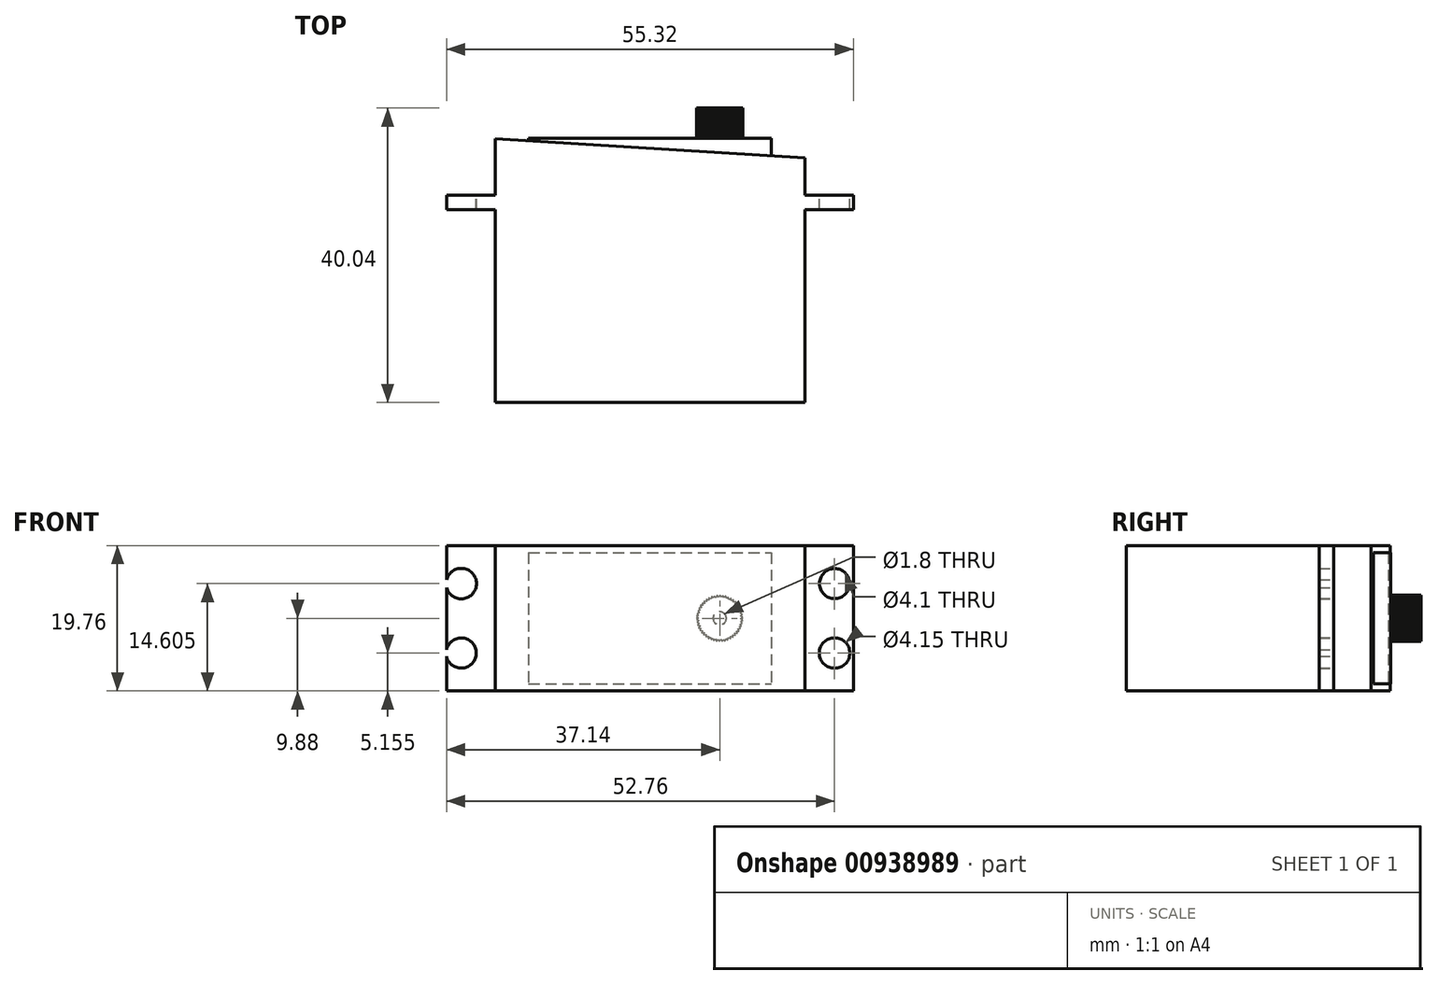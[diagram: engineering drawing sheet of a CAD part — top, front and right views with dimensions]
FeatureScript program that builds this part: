
annotation { "Feature Type Name" : "Feature", "Feature Type Description" : "" }
export const myFeature = defineFeature(function(context is Context, id is Id, definition is map)
    precondition{}
    {
        {
            var Q0;
            Q0=qCreatedBy(makeId("Top.planeOp"),FACE);
            var sketch = newSketch(context, id + "F0", { "sketchPlane" : qUnion([Q0])});
            skLineSegment(sketch, "E0", {"start": v(-4.56, 0) * mm, "end": v(37.56, 0) * mm});
            skLineSegment(sketch, "E1", {"start": v(-4.56, 0) * mm, "end": v(-4.56, 26.2) * mm});
            skLineSegment(sketch, "E2", {"start": v(37.56, 0) * mm, "end": v(37.56, 26.2) * mm});
            skLineSegment(sketch, "E3", {"start": v(-4.56, 35.9) * mm, "end": v(37.56, 33.29) * mm});
            skLineSegment(sketch, "E4", {"start": v(37.56, 0) * mm, "end": v(37.56, 26.2) * mm, "construction": true});
            skLineSegment(sketch, "E5", {"start": v(37.56, 26.2) * mm, "end": v(-4.56, 26.2) * mm, "construction": true});
            skLineSegment(sketch, "E6.bottom", {"start": v(-4.56, 26.2) * mm, "end": v(-11.16, 26.2) * mm});
            skLineSegment(sketch, "E6.top", {"start": v(-4.56, 28.2) * mm, "end": v(-11.16, 28.2) * mm});
            skLineSegment(sketch, "E6.right", {"start": v(-11.16, 26.2) * mm, "end": v(-11.16, 28.2) * mm});
            skLineSegment(sketch, "E7.bottom", {"start": v(37.56, 26.2) * mm, "end": v(44.16, 26.2) * mm});
            skLineSegment(sketch, "E7.top", {"start": v(37.56, 28.2) * mm, "end": v(44.16, 28.2) * mm});
            skLineSegment(sketch, "E7.right", {"start": v(44.16, 26.2) * mm, "end": v(44.16, 28.2) * mm});
            skLineSegment(sketch, "E8.trimOffspring", {"start": v(37.56, 28.2) * mm, "end": v(37.56, 33.29) * mm});
            skLineSegment(sketch, "E9.trimOffspring", {"start": v(-4.56, 28.2) * mm, "end": v(-4.56, 35.9) * mm});
            skLineSegment(sketch, "E10", {"start": v(16.5, 0) * mm, "end": v(16.5, 35.9) * mm, "construction": true});
            skLineSegment(sketch, "E11", {"start": v(0, 35.9) * mm, "end": v(33, 35.9) * mm});
            skLineSegment(sketch, "E12", {"start": v(0, 35.9) * mm, "end": v(0, 35.62) * mm});
            skLineSegment(sketch, "E13", {"start": v(33, 35.9) * mm, "end": v(33, 33.57) * mm});
            skLineSegment(sketch, "E14", {"start": v(37.56, 28.2) * mm, "end": v(-4.56, 28.2) * mm, "construction": true});
            skSolve(sketch);
        }
        {
            var Q0;
            Q0=makeQuery(id+"F0.imprint","IMPRINT",FACE,{"disambiguationData":[TD([[makeQuery(id+"F0.imprint","IMPRINT",EDGE,{"derivedFrom":sQuery(id+"F0.wireOp",EDGE,"E0")}),1.0]])]});
            extrude(context, id + "F1", {"entities" : qUnion([Q0]), "depth" : 19.77 * mm, "offsetDistance" : 25 * mm, "symmetric" : true});
        }
        {
            var Q0;
            Q0=makeQuery(id+"F0.imprint","IMPRINT",FACE,{"disambiguationData":[TD([[makeQuery(id+"F0.imprint","IMPRINT",EDGE,{"derivedFrom":sQuery(id+"F0.wireOp",EDGE,"E11")}),-1.0]])]});
            extrude(context, id + "F2", {"entities" : qUnion([Q0]), "operationType" : NewBodyOperationType.ADD, "depth" : 17.8 * mm, "offsetDistance" : 25 * mm, "symmetric" : true});
        }
        {
            var Q0;
            Q0=makeQuery(id+"F1.opExtrude","SWEPT_FACE",FACE,{"disambiguationData":[OSD([sQuery(id+"F0.wireOp",EDGE,"E7.top")])]});
            var sketch = newSketch(context, id + "F3", { "sketchPlane" : qUnion([Q0])});
            skLineSegment(sketch, "E15", {"start": v(11.16, -4.72) * mm, "end": v(11.16, 4.72) * mm, "construction": true});
            skLineSegment(sketch, "E16", {"start": v(11.16, 4.72) * mm, "end": v(9.16, 4.72) * mm, "construction": true});
            skLineSegment(sketch, "E17", {"start": v(9.16, 4.72) * mm, "end": v(9.16, -4.72) * mm, "construction": true});
            skLineSegment(sketch, "E18", {"start": v(11.16, -4.72) * mm, "end": v(9.16, -4.72) * mm, "construction": true});
            skCircle(sketch, "E19", {"center": v(9.16, -4.72) * mm, "radius": 2.05 * mm});
            skCircle(sketch, "E20", {"center": v(9.16, 4.72) * mm, "radius": 2.08 * mm});
            skLineSegment(sketch, "E21", {"start": v(-43.6, 4.72) * mm, "end": v(-43.6, -4.72) * mm, "construction": true});
            skLineSegment(sketch, "E22", {"start": v(-43.6, -4.72) * mm, "end": v(-41.6, -4.72) * mm, "construction": true});
            skLineSegment(sketch, "E23", {"start": v(-41.6, -4.72) * mm, "end": v(-41.6, 4.73) * mm, "construction": true});
            skLineSegment(sketch, "E24", {"start": v(-43.6, 4.72) * mm, "end": v(-41.6, 4.72) * mm, "construction": true});
            skCircle(sketch, "E25", {"center": v(-41.6, 4.73) * mm, "radius": 2.05 * mm});
            skCircle(sketch, "E26", {"center": v(-41.6, -4.72) * mm, "radius": 2.08 * mm});
            skSolve(sketch);
        }
        {
            var Q0;
            {var subQ0=sQuery(id+"F3.wireOp",EDGE,"E25");var subQ1=makeQuery(id+"F1.opExtrude","SWEPT_EDGE",EDGE,{"disambiguationData":[OSD([sQuery(id+"F0.wireOp",EDGE,"E7.top"),sQuery(id+"F0.wireOp",EDGE,"E7.right")])]});var subQ2=makeQuery(id+"F3.imprint","INTERSECT",VERTEX,{"disambiguationData":[OD(0.0)],"derivedFrom":[subQ1,subQ0]});Q0=makeQuery(id+"F3.imprint","IMPRINT",FACE,{"disambiguationData":[TD([[makeQuery(id+"F3.imprint","IMPRINT",EDGE,{"disambiguationData":[TD([[subQ2,1.0]])],"derivedFrom":subQ0}),1.0]])]});}
            var Q1;
            {var subQ0=sQuery(id+"F3.wireOp",EDGE,"E26");var subQ1=makeQuery(id+"F1.opExtrude","SWEPT_EDGE",EDGE,{"disambiguationData":[OSD([sQuery(id+"F0.wireOp",EDGE,"E7.top"),sQuery(id+"F0.wireOp",EDGE,"E7.right")])]});var subQ2=makeQuery(id+"F3.imprint","INTERSECT",VERTEX,{"disambiguationData":[OD(0.0)],"derivedFrom":[subQ1,subQ0]});Q1=makeQuery(id+"F3.imprint","IMPRINT",FACE,{"disambiguationData":[TD([[makeQuery(id+"F3.imprint","IMPRINT",EDGE,{"disambiguationData":[TD([[subQ2,-1.0]])],"derivedFrom":subQ0}),1.0]])]});}
            var Q2;
            Q2=makeQuery(id+"F3.imprint","IMPRINT",FACE,{"disambiguationData":[TD([[makeQuery(id+"F3.imprint","IMPRINT",EDGE,{"derivedFrom":sQuery(id+"F3.wireOp",EDGE,"E20")}),1.0]])]});
            var Q3;
            Q3=makeQuery(id+"F3.imprint","IMPRINT",FACE,{"disambiguationData":[TD([[makeQuery(id+"F3.imprint","IMPRINT",EDGE,{"derivedFrom":sQuery(id+"F3.wireOp",EDGE,"E19")}),1.0]])]});
            extrude(context, id + "F4", {"entities" : qUnion([Q0, Q1, Q2, Q3]), "operationType" : NewBodyOperationType.REMOVE, "oppositeDirection" : true, "depth" : 25 * mm, "offsetDistance" : 25 * mm});
        }
        {
            var Q0;
            Q0=makeQuery(id+"F2.opExtrude","SWEPT_FACE",FACE,{"disambiguationData":[OSD([sQuery(id+"F0.wireOp",EDGE,"E11")])]});
            var sketch = newSketch(context, id + "F5", { "sketchPlane" : qUnion([Q0])});
            skLineSegment(sketch, "E27", {"start": v(-33, 0) * mm, "end": v(-25.98, 0) * mm, "construction": true});
            skCircle(sketch, "E28", {"center": v(-25.98, 0) * mm, "radius": 2.9 * mm});
            skLineSegment(sketch, "E29", {"start": v(-26.2, 2.9) * mm, "end": v(-26.03, 3.14) * mm});
            skLineSegment(sketch, "E30", {"start": v(-26.03, 3.14) * mm, "end": v(-25.87, 2.9) * mm});
            skLineSegment(sketch, "E31.1.0", {"start": v(-26.56, 2.84) * mm, "end": v(-26.42, 3.1) * mm});
            skLineSegment(sketch, "E31.1.1", {"start": v(-26.42, 3.1) * mm, "end": v(-26.23, 2.89) * mm});
            skLineSegment(sketch, "E31.2.0", {"start": v(-26.91, 2.75) * mm, "end": v(-26.8, 3.03) * mm});
            skLineSegment(sketch, "E31.2.1", {"start": v(-26.8, 3.03) * mm, "end": v(-26.59, 2.84) * mm});
            skLineSegment(sketch, "E31.3.0", {"start": v(-27.25, 2.6) * mm, "end": v(-27.18, 2.9) * mm});
            skLineSegment(sketch, "E31.3.1", {"start": v(-27.18, 2.9) * mm, "end": v(-26.94, 2.74) * mm});
            skLineSegment(sketch, "E31.4.0", {"start": v(-27.57, 2.43) * mm, "end": v(-27.53, 2.73) * mm});
            skLineSegment(sketch, "E31.4.1", {"start": v(-27.53, 2.73) * mm, "end": v(-27.28, 2.6) * mm});
            skLineSegment(sketch, "E31.5.0", {"start": v(-27.86, 2.21) * mm, "end": v(-27.86, 2.51) * mm});
            skLineSegment(sketch, "E31.5.1", {"start": v(-27.86, 2.51) * mm, "end": v(-27.6, 2.41) * mm});
            skLineSegment(sketch, "E31.6.0", {"start": v(-28.12, 1.96) * mm, "end": v(-28.16, 2.26) * mm});
            skLineSegment(sketch, "E31.6.1", {"start": v(-28.16, 2.26) * mm, "end": v(-27.88, 2.2) * mm});
            skLineSegment(sketch, "E31.7.0", {"start": v(-28.35, 1.67) * mm, "end": v(-28.43, 1.96) * mm});
            skLineSegment(sketch, "E31.7.1", {"start": v(-28.43, 1.96) * mm, "end": v(-28.14, 1.94) * mm});
            skLineSegment(sketch, "E31.8.0", {"start": v(-28.54, 1.36) * mm, "end": v(-28.66, 1.64) * mm});
            skLineSegment(sketch, "E31.8.1", {"start": v(-28.66, 1.64) * mm, "end": v(-28.37, 1.65) * mm});
            skLineSegment(sketch, "E31.9.0", {"start": v(-28.69, 1.03) * mm, "end": v(-28.84, 1.3) * mm});
            skLineSegment(sketch, "E31.9.1", {"start": v(-28.84, 1.3) * mm, "end": v(-28.55, 1.34) * mm});
            skLineSegment(sketch, "E31.10.0", {"start": v(-28.8, 0.69) * mm, "end": v(-28.98, 0.92) * mm});
            skLineSegment(sketch, "E31.10.1", {"start": v(-28.98, 0.92) * mm, "end": v(-28.7, 1) * mm});
            skLineSegment(sketch, "E31.11.0", {"start": v(-28.86, 0.33) * mm, "end": v(-29.07, 0.54) * mm});
            skLineSegment(sketch, "E31.11.1", {"start": v(-29.07, 0.54) * mm, "end": v(-28.8, 0.66) * mm});
            skLineSegment(sketch, "E32.3.12.0", {"start": v(-29.12, 0.15) * mm, "end": v(-28.87, 0.3) * mm});
            skLineSegment(sketch, "E32.5.12.0", {"start": v(-28.88, -0.04) * mm, "end": v(-29.12, 0.15) * mm});
            skLineSegment(sketch, "E32.3.13.0", {"start": v(-29.11, -0.24) * mm, "end": v(-28.88, -0.07) * mm});
            skLineSegment(sketch, "E32.5.13.0", {"start": v(-28.85, -0.4) * mm, "end": v(-29.11, -0.24) * mm});
            skLineSegment(sketch, "E32.3.14.0", {"start": v(-29.06, -0.64) * mm, "end": v(-28.85, -0.43) * mm});
            skLineSegment(sketch, "E32.5.14.0", {"start": v(-28.78, -0.76) * mm, "end": v(-29.06, -0.64) * mm});
            skLineSegment(sketch, "E32.3.15.0", {"start": v(-28.95, -1.02) * mm, "end": v(-28.77, -0.79) * mm});
            skLineSegment(sketch, "E32.5.15.0", {"start": v(-28.66, -1.1) * mm, "end": v(-28.95, -1.02) * mm});
            skLineSegment(sketch, "E32.3.16.0", {"start": v(-28.8, -1.38) * mm, "end": v(-28.65, -1.13) * mm});
            skLineSegment(sketch, "E32.5.16.0", {"start": v(-28.5, -1.43) * mm, "end": v(-28.8, -1.38) * mm});
            skLineSegment(sketch, "E32.3.17.0", {"start": v(-28.6, -1.72) * mm, "end": v(-28.49, -1.46) * mm});
            skLineSegment(sketch, "E32.5.17.0", {"start": v(-28.3, -1.73) * mm, "end": v(-28.6, -1.72) * mm});
            skLineSegment(sketch, "E32.3.18.0", {"start": v(-28.37, -2.04) * mm, "end": v(-28.29, -1.76) * mm});
            skLineSegment(sketch, "E32.5.18.0", {"start": v(-28.07, -2.01) * mm, "end": v(-28.37, -2.04) * mm});
            skLineSegment(sketch, "E32.3.19.0", {"start": v(-28.1, -2.32) * mm, "end": v(-28.05, -2.03) * mm});
            skLineSegment(sketch, "E32.5.19.0", {"start": v(-27.8, -2.26) * mm, "end": v(-28.1, -2.32) * mm});
            skLineSegment(sketch, "E33.3.20.0", {"start": v(-27.79, -2.57) * mm, "end": v(-27.78, -2.28) * mm});
            skLineSegment(sketch, "E33.5.20.0", {"start": v(-27.5, -2.47) * mm, "end": v(-27.79, -2.57) * mm});
            skLineSegment(sketch, "E33.3.21.0", {"start": v(-27.45, -2.77) * mm, "end": v(-27.48, -2.48) * mm});
            skLineSegment(sketch, "E33.5.21.0", {"start": v(-27.18, -2.64) * mm, "end": v(-27.45, -2.77) * mm});
            skLineSegment(sketch, "E33.3.22.0", {"start": v(-27.1, -2.94) * mm, "end": v(-27.15, -2.65) * mm});
            skLineSegment(sketch, "E33.5.22.0", {"start": v(-26.84, -2.77) * mm, "end": v(-27.1, -2.94) * mm});
            skLineSegment(sketch, "E33.3.23.0", {"start": v(-26.71, -3.05) * mm, "end": v(-26.81, -2.78) * mm});
            skLineSegment(sketch, "E33.5.23.0", {"start": v(-26.49, -2.86) * mm, "end": v(-26.71, -3.05) * mm});
            skLineSegment(sketch, "E33.3.24.0", {"start": v(-26.33, -3.12) * mm, "end": v(-26.46, -2.86) * mm});
            skLineSegment(sketch, "E33.5.24.0", {"start": v(-26.13, -2.9) * mm, "end": v(-26.33, -3.12) * mm});
            skLineSegment(sketch, "E33.3.25.0", {"start": v(-25.93, -3.14) * mm, "end": v(-26.1, -2.9) * mm});
            skLineSegment(sketch, "E33.5.25.0", {"start": v(-25.76, -2.9) * mm, "end": v(-25.93, -3.14) * mm});
            skLineSegment(sketch, "E33.3.26.0", {"start": v(-25.54, -3.1) * mm, "end": v(-25.73, -2.89) * mm});
            skLineSegment(sketch, "E33.5.26.0", {"start": v(-25.4, -2.84) * mm, "end": v(-25.54, -3.1) * mm});
            skLineSegment(sketch, "E33.3.27.0", {"start": v(-25.15, -3.03) * mm, "end": v(-25.37, -2.84) * mm});
            skLineSegment(sketch, "E33.5.27.0", {"start": v(-25.05, -2.75) * mm, "end": v(-25.15, -3.03) * mm});
            skLineSegment(sketch, "E33.3.28.0", {"start": v(-24.78, -2.9) * mm, "end": v(-25.02, -2.74) * mm});
            skLineSegment(sketch, "E33.5.28.0", {"start": v(-24.71, -2.6) * mm, "end": v(-24.78, -2.9) * mm});
            skLineSegment(sketch, "E33.3.29.0", {"start": v(-24.43, -2.73) * mm, "end": v(-24.68, -2.6) * mm});
            skLineSegment(sketch, "E33.5.29.0", {"start": v(-24.4, -2.43) * mm, "end": v(-24.43, -2.73) * mm});
            skLineSegment(sketch, "E33.3.30.0", {"start": v(-24.1, -2.51) * mm, "end": v(-24.37, -2.41) * mm});
            skLineSegment(sketch, "E33.5.30.0", {"start": v(-24.1, -2.21) * mm, "end": v(-24.1, -2.51) * mm});
            skLineSegment(sketch, "E33.3.31.0", {"start": v(-23.8, -2.26) * mm, "end": v(-24.08, -2.2) * mm});
            skLineSegment(sketch, "E33.5.31.0", {"start": v(-23.84, -1.96) * mm, "end": v(-23.8, -2.26) * mm});
            skLineSegment(sketch, "E33.3.32.0", {"start": v(-23.53, -1.96) * mm, "end": v(-23.82, -1.94) * mm});
            skLineSegment(sketch, "E33.5.32.0", {"start": v(-23.61, -1.67) * mm, "end": v(-23.53, -1.96) * mm});
            skLineSegment(sketch, "E33.3.33.0", {"start": v(-23.3, -1.64) * mm, "end": v(-23.6, -1.65) * mm});
            skLineSegment(sketch, "E33.5.33.0", {"start": v(-23.42, -1.36) * mm, "end": v(-23.3, -1.64) * mm});
            skLineSegment(sketch, "E33.3.34.0", {"start": v(-23.12, -1.3) * mm, "end": v(-23.4, -1.34) * mm});
            skLineSegment(sketch, "E33.5.34.0", {"start": v(-23.27, -1.03) * mm, "end": v(-23.12, -1.3) * mm});
            skLineSegment(sketch, "E33.3.35.0", {"start": v(-22.98, -0.92) * mm, "end": v(-23.26, -1) * mm});
            skLineSegment(sketch, "E33.5.35.0", {"start": v(-23.16, -0.69) * mm, "end": v(-22.98, -0.92) * mm});
            skLineSegment(sketch, "E33.3.36.0", {"start": v(-22.89, -0.54) * mm, "end": v(-23.16, -0.66) * mm});
            skLineSegment(sketch, "E33.5.36.0", {"start": v(-23.1, -0.33) * mm, "end": v(-22.89, -0.54) * mm});
            skLineSegment(sketch, "E33.3.37.0", {"start": v(-22.84, -0.15) * mm, "end": v(-23.1, -0.3) * mm});
            skLineSegment(sketch, "E33.5.37.0", {"start": v(-23.08, 0.04) * mm, "end": v(-22.84, -0.15) * mm});
            skLineSegment(sketch, "E33.3.38.0", {"start": v(-22.85, 0.24) * mm, "end": v(-23.08, 0.07) * mm});
            skLineSegment(sketch, "E33.5.38.0", {"start": v(-23.1, 0.4) * mm, "end": v(-22.85, 0.24) * mm});
            skLineSegment(sketch, "E33.3.39.0", {"start": v(-22.9, 0.64) * mm, "end": v(-23.11, 0.43) * mm});
            skLineSegment(sketch, "E33.5.39.0", {"start": v(-23.18, 0.76) * mm, "end": v(-22.9, 0.64) * mm});
            skLineSegment(sketch, "E34.3.40.0", {"start": v(-23, 1.02) * mm, "end": v(-23.19, 0.79) * mm});
            skLineSegment(sketch, "E34.5.40.0", {"start": v(-23.3, 1.1) * mm, "end": v(-23, 1.02) * mm});
            skLineSegment(sketch, "E34.3.41.0", {"start": v(-23.16, 1.38) * mm, "end": v(-23.3, 1.13) * mm});
            skLineSegment(sketch, "E34.5.41.0", {"start": v(-23.46, 1.43) * mm, "end": v(-23.16, 1.38) * mm});
            skLineSegment(sketch, "E34.3.42.0", {"start": v(-23.35, 1.72) * mm, "end": v(-23.47, 1.46) * mm});
            skLineSegment(sketch, "E34.5.42.0", {"start": v(-23.66, 1.73) * mm, "end": v(-23.35, 1.72) * mm});
            skLineSegment(sketch, "E34.3.43.0", {"start": v(-23.6, 2.04) * mm, "end": v(-23.67, 1.76) * mm});
            skLineSegment(sketch, "E34.5.43.0", {"start": v(-23.9, 2.01) * mm, "end": v(-23.6, 2.04) * mm});
            skLineSegment(sketch, "E34.3.44.0", {"start": v(-23.87, 2.32) * mm, "end": v(-23.91, 2.03) * mm});
            skLineSegment(sketch, "E34.5.44.0", {"start": v(-24.16, 2.26) * mm, "end": v(-23.87, 2.32) * mm});
            skLineSegment(sketch, "E35.3.45.0", {"start": v(-24.17, 2.57) * mm, "end": v(-24.18, 2.28) * mm});
            skLineSegment(sketch, "E35.5.45.0", {"start": v(-24.46, 2.47) * mm, "end": v(-24.17, 2.57) * mm});
            skLineSegment(sketch, "E35.3.46.0", {"start": v(-24.5, 2.77) * mm, "end": v(-24.48, 2.48) * mm});
            skLineSegment(sketch, "E35.5.46.0", {"start": v(-24.78, 2.64) * mm, "end": v(-24.5, 2.77) * mm});
            skLineSegment(sketch, "E35.3.47.0", {"start": v(-24.87, 2.94) * mm, "end": v(-24.8, 2.65) * mm});
            skLineSegment(sketch, "E35.5.47.0", {"start": v(-25.12, 2.77) * mm, "end": v(-24.87, 2.94) * mm});
            skLineSegment(sketch, "E35.3.48.0", {"start": v(-25.25, 3.05) * mm, "end": v(-25.15, 2.78) * mm});
            skLineSegment(sketch, "E35.5.48.0", {"start": v(-25.47, 2.86) * mm, "end": v(-25.25, 3.05) * mm});
            skLineSegment(sketch, "E35.3.49.0", {"start": v(-25.63, 3.12) * mm, "end": v(-25.5, 2.86) * mm});
            skLineSegment(sketch, "E35.5.49.0", {"start": v(-25.83, 2.9) * mm, "end": v(-25.63, 3.12) * mm});
            skCircle(sketch, "E36", {"center": v(-25.98, 0) * mm, "radius": 0.9 * mm});
            skSolve(sketch);
        }
        {
            var Q0;
            {var subQ0=sQuery(id+"F5.wireOp",EDGE,"E31.9.0");Q0=makeQuery(id+"F5.imprint","IMPRINT",FACE,{"disambiguationData":[TD([[makeQuery(id+"F5.imprint","IMPRINT",EDGE,{"derivedFrom":subQ0}),-1.0]])]});}
            var Q1;
            {var subQ0=sQuery(id+"F5.wireOp",EDGE,"E31.8.0");Q1=makeQuery(id+"F5.imprint","IMPRINT",FACE,{"disambiguationData":[TD([[makeQuery(id+"F5.imprint","IMPRINT",EDGE,{"derivedFrom":subQ0}),-1.0]])]});}
            var Q2;
            {var subQ0=sQuery(id+"F5.wireOp",EDGE,"E31.7.0");Q2=makeQuery(id+"F5.imprint","IMPRINT",FACE,{"disambiguationData":[TD([[makeQuery(id+"F5.imprint","IMPRINT",EDGE,{"derivedFrom":subQ0}),-1.0]])]});}
            var Q3;
            {var subQ0=sQuery(id+"F5.wireOp",EDGE,"E31.6.0");Q3=makeQuery(id+"F5.imprint","IMPRINT",FACE,{"disambiguationData":[TD([[makeQuery(id+"F5.imprint","IMPRINT",EDGE,{"derivedFrom":subQ0}),-1.0]])]});}
            var Q4;
            {var subQ0=sQuery(id+"F5.wireOp",EDGE,"E31.5.0");Q4=makeQuery(id+"F5.imprint","IMPRINT",FACE,{"disambiguationData":[TD([[makeQuery(id+"F5.imprint","IMPRINT",EDGE,{"derivedFrom":subQ0}),-1.0]])]});}
            var Q5;
            {var subQ0=sQuery(id+"F5.wireOp",EDGE,"E31.4.0");Q5=makeQuery(id+"F5.imprint","IMPRINT",FACE,{"disambiguationData":[TD([[makeQuery(id+"F5.imprint","IMPRINT",EDGE,{"derivedFrom":subQ0}),-1.0]])]});}
            var Q6;
            {var subQ0=sQuery(id+"F5.wireOp",EDGE,"E31.3.0");Q6=makeQuery(id+"F5.imprint","IMPRINT",FACE,{"disambiguationData":[TD([[makeQuery(id+"F5.imprint","IMPRINT",EDGE,{"derivedFrom":subQ0}),-1.0]])]});}
            var Q7;
            {var subQ0=sQuery(id+"F5.wireOp",EDGE,"E31.2.0");Q7=makeQuery(id+"F5.imprint","IMPRINT",FACE,{"disambiguationData":[TD([[makeQuery(id+"F5.imprint","IMPRINT",EDGE,{"derivedFrom":subQ0}),-1.0]])]});}
            var Q8;
            {var subQ0=sQuery(id+"F5.wireOp",EDGE,"E31.1.0");Q8=makeQuery(id+"F5.imprint","IMPRINT",FACE,{"disambiguationData":[TD([[makeQuery(id+"F5.imprint","IMPRINT",EDGE,{"derivedFrom":subQ0}),-1.0]])]});}
            var Q9;
            {var subQ0=sQuery(id+"F5.wireOp",EDGE,"E29");Q9=makeQuery(id+"F5.imprint","IMPRINT",FACE,{"disambiguationData":[TD([[makeQuery(id+"F5.imprint","IMPRINT",EDGE,{"derivedFrom":subQ0}),-1.0]])]});}
            var Q10;
            {var subQ0=sQuery(id+"F5.wireOp",EDGE,"E35.3.49.0");Q10=makeQuery(id+"F5.imprint","IMPRINT",FACE,{"disambiguationData":[TD([[makeQuery(id+"F5.imprint","IMPRINT",EDGE,{"derivedFrom":subQ0}),-1.0]])]});}
            var Q11;
            {var subQ0=sQuery(id+"F5.wireOp",EDGE,"E35.3.48.0");Q11=makeQuery(id+"F5.imprint","IMPRINT",FACE,{"disambiguationData":[TD([[makeQuery(id+"F5.imprint","IMPRINT",EDGE,{"derivedFrom":subQ0}),-1.0]])]});}
            var Q12;
            {var subQ0=sQuery(id+"F5.wireOp",EDGE,"E35.3.47.0");Q12=makeQuery(id+"F5.imprint","IMPRINT",FACE,{"disambiguationData":[TD([[makeQuery(id+"F5.imprint","IMPRINT",EDGE,{"derivedFrom":subQ0}),-1.0]])]});}
            var Q13;
            {var subQ0=sQuery(id+"F5.wireOp",EDGE,"E35.3.46.0");Q13=makeQuery(id+"F5.imprint","IMPRINT",FACE,{"disambiguationData":[TD([[makeQuery(id+"F5.imprint","IMPRINT",EDGE,{"derivedFrom":subQ0}),-1.0]])]});}
            var Q14;
            {var subQ0=sQuery(id+"F5.wireOp",EDGE,"E35.3.45.0");Q14=makeQuery(id+"F5.imprint","IMPRINT",FACE,{"disambiguationData":[TD([[makeQuery(id+"F5.imprint","IMPRINT",EDGE,{"derivedFrom":subQ0}),-1.0]])]});}
            var Q15;
            {var subQ0=sQuery(id+"F5.wireOp",EDGE,"E34.3.44.0");Q15=makeQuery(id+"F5.imprint","IMPRINT",FACE,{"disambiguationData":[TD([[makeQuery(id+"F5.imprint","IMPRINT",EDGE,{"derivedFrom":subQ0}),-1.0]])]});}
            var Q16;
            {var subQ0=sQuery(id+"F5.wireOp",EDGE,"E34.3.43.0");Q16=makeQuery(id+"F5.imprint","IMPRINT",FACE,{"disambiguationData":[TD([[makeQuery(id+"F5.imprint","IMPRINT",EDGE,{"derivedFrom":subQ0}),-1.0]])]});}
            var Q17;
            {var subQ0=sQuery(id+"F5.wireOp",EDGE,"E34.3.42.0");Q17=makeQuery(id+"F5.imprint","IMPRINT",FACE,{"disambiguationData":[TD([[makeQuery(id+"F5.imprint","IMPRINT",EDGE,{"derivedFrom":subQ0}),-1.0]])]});}
            var Q18;
            {var subQ0=sQuery(id+"F5.wireOp",EDGE,"E34.3.41.0");Q18=makeQuery(id+"F5.imprint","IMPRINT",FACE,{"disambiguationData":[TD([[makeQuery(id+"F5.imprint","IMPRINT",EDGE,{"derivedFrom":subQ0}),-1.0]])]});}
            var Q19;
            {var subQ0=sQuery(id+"F5.wireOp",EDGE,"E34.3.40.0");Q19=makeQuery(id+"F5.imprint","IMPRINT",FACE,{"disambiguationData":[TD([[makeQuery(id+"F5.imprint","IMPRINT",EDGE,{"derivedFrom":subQ0}),-1.0]])]});}
            var Q20;
            {var subQ0=sQuery(id+"F5.wireOp",EDGE,"E33.3.39.0");Q20=makeQuery(id+"F5.imprint","IMPRINT",FACE,{"disambiguationData":[TD([[makeQuery(id+"F5.imprint","IMPRINT",EDGE,{"derivedFrom":subQ0}),-1.0]])]});}
            var Q21;
            {var subQ0=sQuery(id+"F5.wireOp",EDGE,"E33.3.38.0");Q21=makeQuery(id+"F5.imprint","IMPRINT",FACE,{"disambiguationData":[TD([[makeQuery(id+"F5.imprint","IMPRINT",EDGE,{"derivedFrom":subQ0}),-1.0]])]});}
            var Q22;
            {var subQ0=sQuery(id+"F5.wireOp",EDGE,"E33.3.37.0");Q22=makeQuery(id+"F5.imprint","IMPRINT",FACE,{"disambiguationData":[TD([[makeQuery(id+"F5.imprint","IMPRINT",EDGE,{"derivedFrom":subQ0}),-1.0]])]});}
            var Q23;
            {var subQ0=sQuery(id+"F5.wireOp",EDGE,"E33.3.36.0");Q23=makeQuery(id+"F5.imprint","IMPRINT",FACE,{"disambiguationData":[TD([[makeQuery(id+"F5.imprint","IMPRINT",EDGE,{"derivedFrom":subQ0}),-1.0]])]});}
            var Q24;
            {var subQ0=sQuery(id+"F5.wireOp",EDGE,"E33.3.35.0");Q24=makeQuery(id+"F5.imprint","IMPRINT",FACE,{"disambiguationData":[TD([[makeQuery(id+"F5.imprint","IMPRINT",EDGE,{"derivedFrom":subQ0}),-1.0]])]});}
            var Q25;
            {var subQ0=sQuery(id+"F5.wireOp",EDGE,"E33.3.34.0");Q25=makeQuery(id+"F5.imprint","IMPRINT",FACE,{"disambiguationData":[TD([[makeQuery(id+"F5.imprint","IMPRINT",EDGE,{"derivedFrom":subQ0}),-1.0]])]});}
            var Q26;
            {var subQ0=sQuery(id+"F5.wireOp",EDGE,"E33.3.33.0");Q26=makeQuery(id+"F5.imprint","IMPRINT",FACE,{"disambiguationData":[TD([[makeQuery(id+"F5.imprint","IMPRINT",EDGE,{"derivedFrom":subQ0}),-1.0]])]});}
            var Q27;
            {var subQ0=sQuery(id+"F5.wireOp",EDGE,"E33.3.32.0");Q27=makeQuery(id+"F5.imprint","IMPRINT",FACE,{"disambiguationData":[TD([[makeQuery(id+"F5.imprint","IMPRINT",EDGE,{"derivedFrom":subQ0}),-1.0]])]});}
            var Q28;
            {var subQ0=sQuery(id+"F5.wireOp",EDGE,"E33.3.31.0");Q28=makeQuery(id+"F5.imprint","IMPRINT",FACE,{"disambiguationData":[TD([[makeQuery(id+"F5.imprint","IMPRINT",EDGE,{"derivedFrom":subQ0}),-1.0]])]});}
            var Q29;
            {var subQ0=sQuery(id+"F5.wireOp",EDGE,"E33.3.30.0");Q29=makeQuery(id+"F5.imprint","IMPRINT",FACE,{"disambiguationData":[TD([[makeQuery(id+"F5.imprint","IMPRINT",EDGE,{"derivedFrom":subQ0}),-1.0]])]});}
            var Q30;
            {var subQ0=sQuery(id+"F5.wireOp",EDGE,"E33.3.29.0");Q30=makeQuery(id+"F5.imprint","IMPRINT",FACE,{"disambiguationData":[TD([[makeQuery(id+"F5.imprint","IMPRINT",EDGE,{"derivedFrom":subQ0}),-1.0]])]});}
            var Q31;
            {var subQ0=sQuery(id+"F5.wireOp",EDGE,"E33.3.28.0");Q31=makeQuery(id+"F5.imprint","IMPRINT",FACE,{"disambiguationData":[TD([[makeQuery(id+"F5.imprint","IMPRINT",EDGE,{"derivedFrom":subQ0}),-1.0]])]});}
            var Q32;
            {var subQ0=sQuery(id+"F5.wireOp",EDGE,"E33.3.27.0");Q32=makeQuery(id+"F5.imprint","IMPRINT",FACE,{"disambiguationData":[TD([[makeQuery(id+"F5.imprint","IMPRINT",EDGE,{"derivedFrom":subQ0}),-1.0]])]});}
            var Q33;
            {var subQ0=sQuery(id+"F5.wireOp",EDGE,"E33.3.26.0");Q33=makeQuery(id+"F5.imprint","IMPRINT",FACE,{"disambiguationData":[TD([[makeQuery(id+"F5.imprint","IMPRINT",EDGE,{"derivedFrom":subQ0}),-1.0]])]});}
            var Q34;
            {var subQ0=sQuery(id+"F5.wireOp",EDGE,"E33.3.25.0");Q34=makeQuery(id+"F5.imprint","IMPRINT",FACE,{"disambiguationData":[TD([[makeQuery(id+"F5.imprint","IMPRINT",EDGE,{"derivedFrom":subQ0}),-1.0]])]});}
            var Q35;
            {var subQ0=sQuery(id+"F5.wireOp",EDGE,"E33.3.23.0");Q35=makeQuery(id+"F5.imprint","IMPRINT",FACE,{"disambiguationData":[TD([[makeQuery(id+"F5.imprint","IMPRINT",EDGE,{"derivedFrom":subQ0}),-1.0]])]});}
            var Q36;
            {var subQ0=sQuery(id+"F5.wireOp",EDGE,"E31.10.0");Q36=makeQuery(id+"F5.imprint","IMPRINT",FACE,{"disambiguationData":[TD([[makeQuery(id+"F5.imprint","IMPRINT",EDGE,{"derivedFrom":subQ0}),-1.0]])]});}
            var Q37;
            {var subQ0=sQuery(id+"F5.wireOp",EDGE,"E31.11.0");Q37=makeQuery(id+"F5.imprint","IMPRINT",FACE,{"disambiguationData":[TD([[makeQuery(id+"F5.imprint","IMPRINT",EDGE,{"derivedFrom":subQ0}),-1.0]])]});}
            var Q38;
            {var subQ0=sQuery(id+"F5.wireOp",EDGE,"E32.3.13.0");Q38=makeQuery(id+"F5.imprint","IMPRINT",FACE,{"disambiguationData":[TD([[makeQuery(id+"F5.imprint","IMPRINT",EDGE,{"derivedFrom":subQ0}),-1.0]])]});}
            var Q39;
            {var subQ0=sQuery(id+"F5.wireOp",EDGE,"E32.3.14.0");Q39=makeQuery(id+"F5.imprint","IMPRINT",FACE,{"disambiguationData":[TD([[makeQuery(id+"F5.imprint","IMPRINT",EDGE,{"derivedFrom":subQ0}),-1.0]])]});}
            var Q40;
            {var subQ0=sQuery(id+"F5.wireOp",EDGE,"E32.3.15.0");Q40=makeQuery(id+"F5.imprint","IMPRINT",FACE,{"disambiguationData":[TD([[makeQuery(id+"F5.imprint","IMPRINT",EDGE,{"derivedFrom":subQ0}),-1.0]])]});}
            var Q41;
            {var subQ0=sQuery(id+"F5.wireOp",EDGE,"E32.3.16.0");Q41=makeQuery(id+"F5.imprint","IMPRINT",FACE,{"disambiguationData":[TD([[makeQuery(id+"F5.imprint","IMPRINT",EDGE,{"derivedFrom":subQ0}),-1.0]])]});}
            var Q42;
            Q42=makeQuery(id+"F5.imprint","IMPRINT",FACE,{"disambiguationData":[TD([[makeQuery(id+"F5.imprint","IMPRINT",EDGE,{"derivedFrom":sQuery(id+"F5.wireOp",EDGE,"E36")}),-1.0]])]});
            var Q43;
            {var subQ0=sQuery(id+"F5.wireOp",EDGE,"E32.3.17.0");Q43=makeQuery(id+"F5.imprint","IMPRINT",FACE,{"disambiguationData":[TD([[makeQuery(id+"F5.imprint","IMPRINT",EDGE,{"derivedFrom":subQ0}),-1.0]])]});}
            var Q44;
            {var subQ0=sQuery(id+"F5.wireOp",EDGE,"E32.3.18.0");Q44=makeQuery(id+"F5.imprint","IMPRINT",FACE,{"disambiguationData":[TD([[makeQuery(id+"F5.imprint","IMPRINT",EDGE,{"derivedFrom":subQ0}),-1.0]])]});}
            var Q45;
            {var subQ0=sQuery(id+"F5.wireOp",EDGE,"E32.3.19.0");Q45=makeQuery(id+"F5.imprint","IMPRINT",FACE,{"disambiguationData":[TD([[makeQuery(id+"F5.imprint","IMPRINT",EDGE,{"derivedFrom":subQ0}),-1.0]])]});}
            var Q46;
            {var subQ0=sQuery(id+"F5.wireOp",EDGE,"E33.3.20.0");Q46=makeQuery(id+"F5.imprint","IMPRINT",FACE,{"disambiguationData":[TD([[makeQuery(id+"F5.imprint","IMPRINT",EDGE,{"derivedFrom":subQ0}),-1.0]])]});}
            var Q47;
            {var subQ0=sQuery(id+"F5.wireOp",EDGE,"E33.3.21.0");Q47=makeQuery(id+"F5.imprint","IMPRINT",FACE,{"disambiguationData":[TD([[makeQuery(id+"F5.imprint","IMPRINT",EDGE,{"derivedFrom":subQ0}),-1.0]])]});}
            var Q48;
            {var subQ0=sQuery(id+"F5.wireOp",EDGE,"E33.3.22.0");Q48=makeQuery(id+"F5.imprint","IMPRINT",FACE,{"disambiguationData":[TD([[makeQuery(id+"F5.imprint","IMPRINT",EDGE,{"derivedFrom":subQ0}),-1.0]])]});}
            var Q49;
            {var subQ0=sQuery(id+"F5.wireOp",EDGE,"E33.3.24.0");Q49=makeQuery(id+"F5.imprint","IMPRINT",FACE,{"disambiguationData":[TD([[makeQuery(id+"F5.imprint","IMPRINT",EDGE,{"derivedFrom":subQ0}),-1.0]])]});}
            var Q50;
            {var subQ0=sQuery(id+"F5.wireOp",EDGE,"E32.3.12.0");Q50=makeQuery(id+"F5.imprint","IMPRINT",FACE,{"disambiguationData":[TD([[makeQuery(id+"F5.imprint","IMPRINT",EDGE,{"derivedFrom":subQ0}),-1.0]])]});}
            extrude(context, id + "F6", {"entities" : qUnion([Q0, Q1, Q2, Q3, Q4, Q5, Q6, Q7, Q8, Q9, Q10, Q11, Q12, Q13, Q14, Q15, Q16, Q17, Q18, Q19, Q20, Q21, Q22, Q23, Q24, Q25, Q26, Q27, Q28, Q29, Q30, Q31, Q32, Q33, Q34, Q35, Q36, Q37, Q38, Q39, Q40, Q41, Q42, Q43, Q44, Q45, Q46, Q47, Q48, Q49, Q50]), "depth" : 4.13 * mm, "offsetDistance" : 25 * mm});
        }
    });
